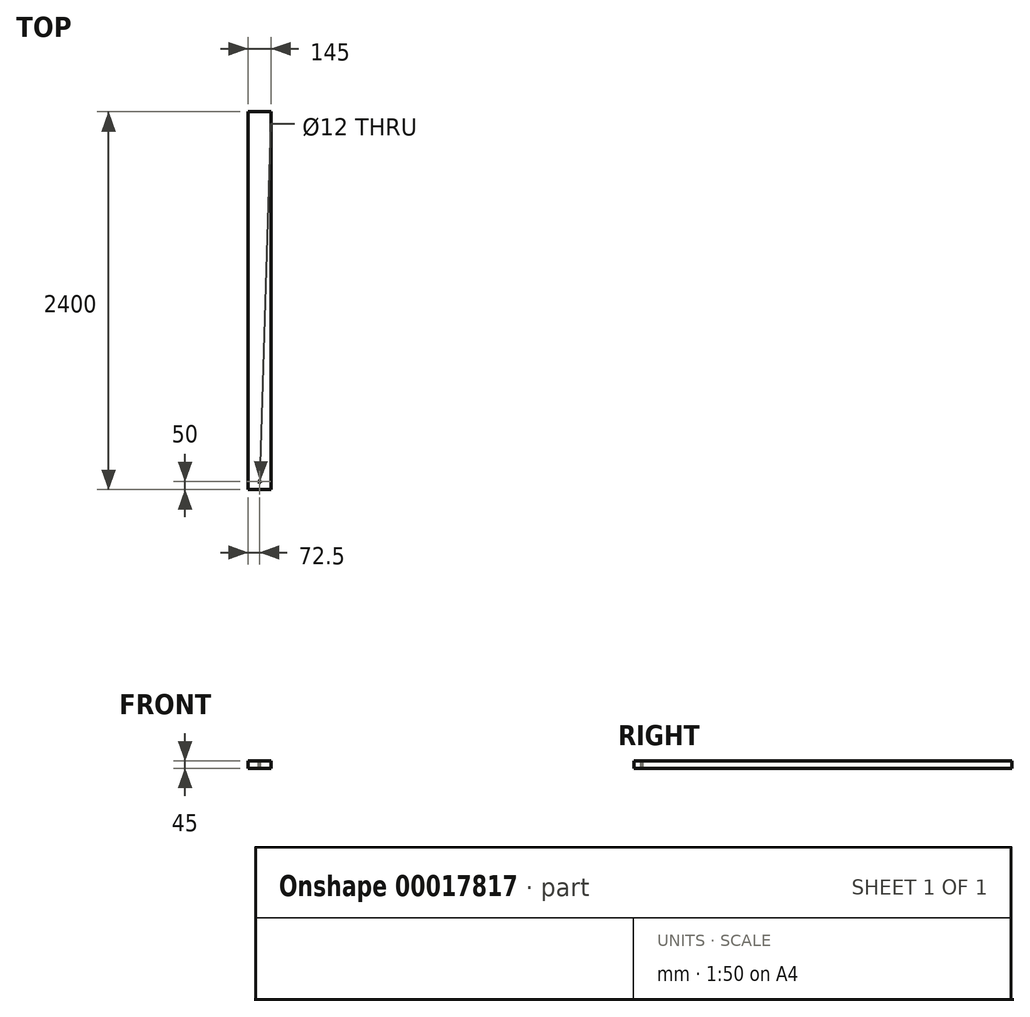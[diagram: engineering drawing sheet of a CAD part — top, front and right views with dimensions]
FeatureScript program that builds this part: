
annotation { "Feature Type Name" : "Feature", "Feature Type Description" : "" }
export const myFeature = defineFeature(function(context is Context, id is Id, definition is map)
    precondition{}
    {
        {
            var Q0;
            Q0=qCreatedBy(makeId("Front.planeOp"),FACE);
            var sketch = newSketch(context, id + "F0", { "sketchPlane" : qUnion([Q0])});
            skLineSegment(sketch, "E0.rect.bottom", {"start": v(-72.5, -22.5) * mm, "end": v(72.5, -22.5) * mm});
            skLineSegment(sketch, "E0.rect.top", {"start": v(-72.5, 22.5) * mm, "end": v(72.5, 22.5) * mm});
            skLineSegment(sketch, "E0.rect.left", {"start": v(-72.5, -22.5) * mm, "end": v(-72.5, 22.5) * mm});
            skLineSegment(sketch, "E0.rect.right", {"start": v(72.5, -22.5) * mm, "end": v(72.5, 22.5) * mm});
            skPoint(sketch, "E0.rect.middle", {"position": v(0, 0) * mm});
            skSolve(sketch);
        }
        {
            var Q0;
            Q0 = qSketchRegion(id + "F0", true);
            extrude(context, id + "F1", {"entities" : qUnion([Q0]), "depth" : 2400 * mm});
        }
        {
            var Q0;
            Q0=makeQuery(id+"F1.opExtrude","SWEPT_FACE",FACE,{"disambiguationData":[OSD([sQuery(id+"F0.wireOp",EDGE,"E0.rect.top")])]});
            var sketch = newSketch(context, id + "F2", { "sketchPlane" : qUnion([Q0])});
            skPoint(sketch, "E1", {"position": v(0, -2350) * mm});
            skSolve(sketch);
        }
        {
            var Q0;
            Q0=sQuery(id+"F2.wireOp",VERTEX,"E1");
            var Q1;
            Q1=makeQuery(id+"F1.opExtrude","SWEPT_BODY",BODY,{"disambiguationData":[OSD([sQuery(id+"F0.wireOp",EDGE,"E0.rect.bottom"),sQuery(id+"F0.wireOp",EDGE,"E0.rect.top"),sQuery(id+"F0.wireOp",EDGE,"E0.rect.left"),sQuery(id+"F0.wireOp",EDGE,"E0.rect.right")])]});
            hole(context, id + "F3", {"style" : HoleStyle.SIMPLE, "holeDiameter" : 12 * mm, "endStyle" : HoleEndStyle.THROUGH, "locations" : qUnion([Q0]), "scope" : qUnion([Q1])});
        }
    });
